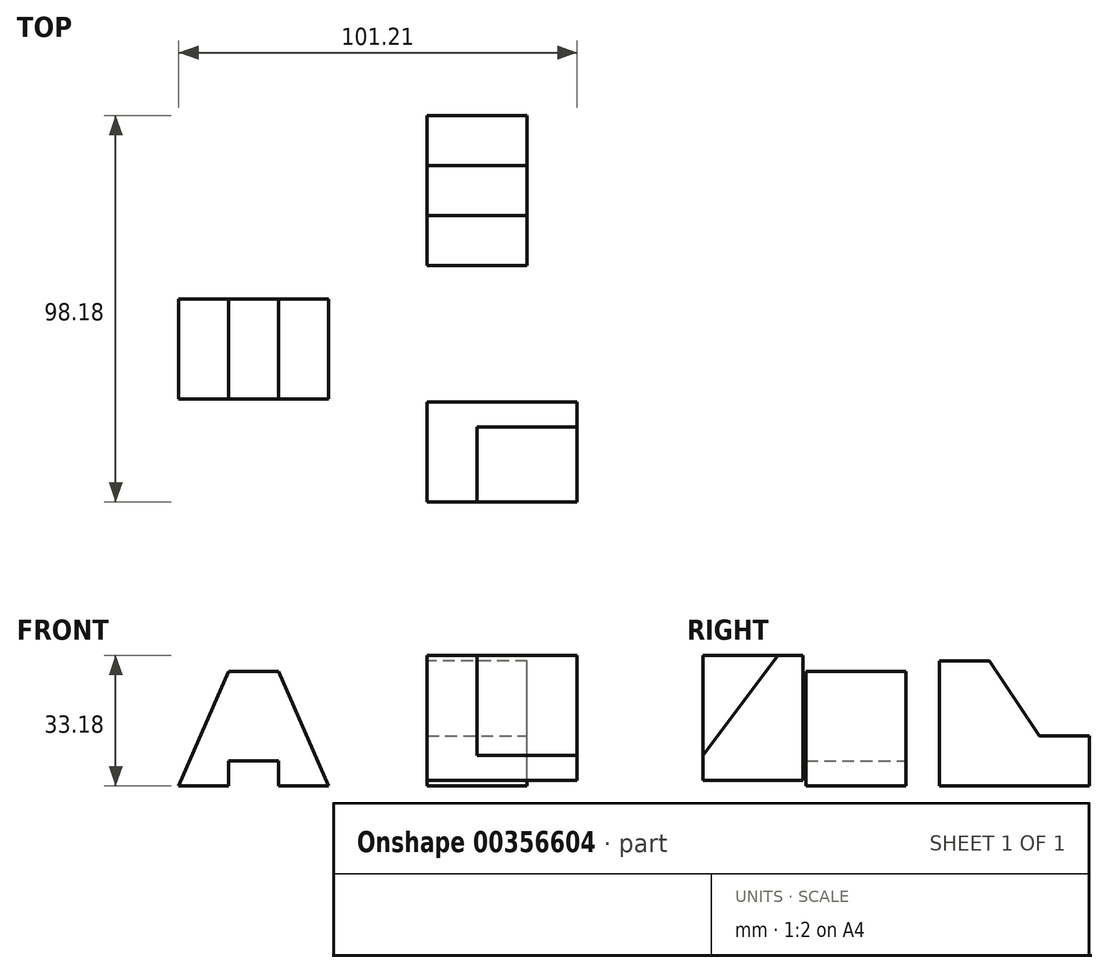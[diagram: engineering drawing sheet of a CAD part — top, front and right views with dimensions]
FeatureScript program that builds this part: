
annotation { "Feature Type Name" : "Feature", "Feature Type Description" : "" }
export const myFeature = defineFeature(function(context is Context, id is Id, definition is map)
    precondition{}
    {
        {
            var Q0;
            Q0=qCreatedBy(makeId("Right.planeOp"),FACE);
            var sketch = newSketch(context, id + "F0", { "sketchPlane" : qUnion([Q0])});
            skLineSegment(sketch, "E0.bottom", {"start": v(-51.59, 33.18) * mm, "end": v(-26.19, 33.18) * mm});
            skLineSegment(sketch, "E0.top", {"start": v(-51.59, 1.43) * mm, "end": v(-26.19, 1.43) * mm});
            skLineSegment(sketch, "E0.left", {"start": v(-51.59, 33.18) * mm, "end": v(-51.59, 1.43) * mm});
            skLineSegment(sketch, "E0.right", {"start": v(-26.19, 33.18) * mm, "end": v(-26.19, 1.43) * mm});
            skSolve(sketch);
        }
        {
            var Q0;
            Q0 = qSketchRegion(id + "F0", true);
            extrude(context, id + "F1", {"entities" : qUnion([Q0]), "depth" : 38.1 * mm});
        }
        {
            var Q0;
            Q0=makeQuery(id+"F1.opExtrude","CAP_FACE",FACE,{"disambiguationData":[OSD([sQuery(id+"F0.wireOp",EDGE,"E0.bottom"),sQuery(id+"F0.wireOp",EDGE,"E0.top"),sQuery(id+"F0.wireOp",EDGE,"E0.left"),sQuery(id+"F0.wireOp",EDGE,"E0.right")])],"isStart":false});
            var sketch = newSketch(context, id + "F2", { "sketchPlane" : qUnion([Q0])});
            skLineSegment(sketch, "E1", {"start": v(-32.54, 33.18) * mm, "end": v(-51.59, 7.78) * mm});
            skPoint(sketch, "E2", {"position": v(-51.59, 17.3) * mm});
            skLineSegment(sketch, "E3", {"start": v(-32.54, 33.18) * mm, "end": v(-26.19, 33.18) * mm});
            skLineSegment(sketch, "E4", {"start": v(-26.19, 33.18) * mm, "end": v(-26.19, 1.43) * mm});
            skLineSegment(sketch, "E5", {"start": v(-26.19, 1.43) * mm, "end": v(-51.59, 1.43) * mm});
            skLineSegment(sketch, "E6", {"start": v(-51.59, 1.43) * mm, "end": v(-51.59, 7.78) * mm});
            skSolve(sketch);
        }
        {
            var Q0;
            {var subQ0=sQuery(id+"F2.wireOp",EDGE,"E1");Q0=makeQuery(id+"F2.imprint","IMPRINT",FACE,{"disambiguationData":[TD([[makeQuery(id+"F2.imprint","IMPRINT",EDGE,{"derivedFrom":subQ0}),-1.0]])]});}
            extrude(context, id + "F3", {"entities" : qUnion([Q0]), "operationType" : NewBodyOperationType.REMOVE, "oppositeDirection" : true, "depth" : 25.4 * mm});
        }
        {
            var Q0;
            Q0=qCreatedBy(makeId("Right.planeOp"),FACE);
            var sketch = newSketch(context, id + "F4", { "sketchPlane" : qUnion([Q0])});
            skLineSegment(sketch, "E7.bottom", {"start": v(8.49, 0) * mm, "end": v(46.59, 0) * mm});
            skLineSegment(sketch, "E7.top", {"start": v(8.49, 31.75) * mm, "end": v(46.59, 31.75) * mm});
            skLineSegment(sketch, "E7.left", {"start": v(8.49, 0) * mm, "end": v(8.49, 31.75) * mm});
            skLineSegment(sketch, "E7.right", {"start": v(46.59, 0) * mm, "end": v(46.59, 31.75) * mm});
            skSolve(sketch);
        }
        {
            var Q0;
            Q0 = qSketchRegion(id + "F4", true);
            extrude(context, id + "F5", {"entities" : qUnion([Q0]), "depth" : 25.4 * mm});
        }
        {
            var Q0;
            Q0=makeQuery(id+"F5.opExtrude","CAP_FACE",FACE,{"disambiguationData":[OSD([sQuery(id+"F4.wireOp",EDGE,"E7.bottom"),sQuery(id+"F4.wireOp",EDGE,"E7.top"),sQuery(id+"F4.wireOp",EDGE,"E7.left"),sQuery(id+"F4.wireOp",EDGE,"E7.right")])],"isStart":false});
            var sketch = newSketch(context, id + "F6", { "sketchPlane" : qUnion([Q0])});
            skLineSegment(sketch, "E8", {"start": v(46.59, 12.7) * mm, "end": v(46.59, 0) * mm});
            skLineSegment(sketch, "E9", {"start": v(46.59, 0) * mm, "end": v(8.49, 0) * mm});
            skLineSegment(sketch, "E10", {"start": v(8.49, 0) * mm, "end": v(8.49, 31.75) * mm});
            skLineSegment(sketch, "E11", {"start": v(8.49, 31.75) * mm, "end": v(21.19, 31.75) * mm});
            skLineSegment(sketch, "E12", {"start": v(46.59, 12.7) * mm, "end": v(33.89, 12.7) * mm});
            skLineSegment(sketch, "E13", {"start": v(33.89, 12.7) * mm, "end": v(21.19, 31.75) * mm});
            skSolve(sketch);
        }
        {
            var Q0;
            {var subQ0=sQuery(id+"F6.wireOp",EDGE,"E12");Q0=makeQuery(id+"F6.imprint","IMPRINT",FACE,{"disambiguationData":[TD([[makeQuery(id+"F6.imprint","IMPRINT",EDGE,{"derivedFrom":subQ0}),-1.0]])]});}
            extrude(context, id + "F7", {"entities" : qUnion([Q0]), "operationType" : NewBodyOperationType.REMOVE, "oppositeDirection" : true, "depth" : 25.4 * mm});
        }
        {
            var Q0;
            Q0=qCreatedBy(makeId("Front.planeOp"),FACE);
            var sketch = newSketch(context, id + "F8", { "sketchPlane" : qUnion([Q0])});
            skLineSegment(sketch, "E14", {"start": v(-63.11, 0) * mm, "end": v(-50.41, 29.1) * mm});
            skLineSegment(sketch, "E15", {"start": v(-50.41, 29.1) * mm, "end": v(-37.71, 29.1) * mm});
            skLineSegment(sketch, "E16", {"start": v(-37.71, 29.1) * mm, "end": v(-25.01, 0) * mm});
            skLineSegment(sketch, "E17", {"start": v(-25.01, 0) * mm, "end": v(-37.71, 0) * mm});
            skLineSegment(sketch, "E18", {"start": v(-37.71, 0) * mm, "end": v(-37.71, 6.35) * mm});
            skLineSegment(sketch, "E19", {"start": v(-37.71, 6.35) * mm, "end": v(-50.41, 6.35) * mm});
            skLineSegment(sketch, "E20", {"start": v(-50.41, 6.35) * mm, "end": v(-50.41, 0) * mm});
            skLineSegment(sketch, "E21", {"start": v(-50.41, 0) * mm, "end": v(-63.11, 0) * mm});
            skSolve(sketch);
        }
        {
            var Q0;
            Q0 = qSketchRegion(id + "F8", true);
            extrude(context, id + "F9", {"entities" : qUnion([Q0]), "depth" : 25.4 * mm});
        }
    });
